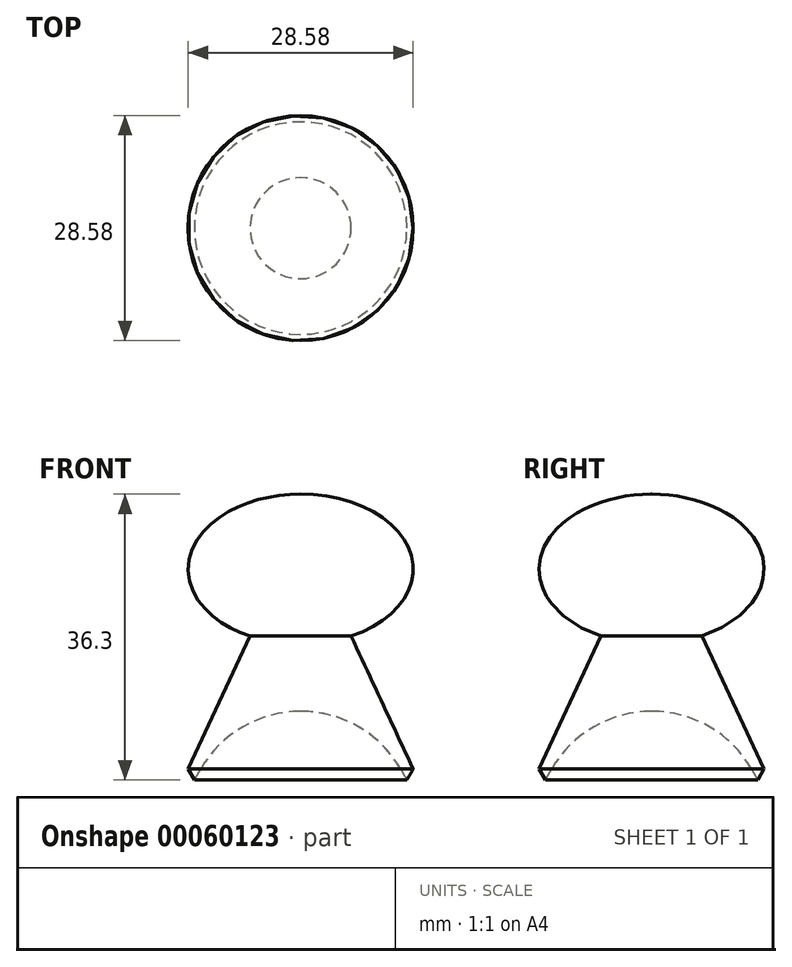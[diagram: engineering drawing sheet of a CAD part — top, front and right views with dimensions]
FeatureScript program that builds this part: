
annotation { "Feature Type Name" : "Feature", "Feature Type Description" : "" }
export const myFeature = defineFeature(function(context is Context, id is Id, definition is map)
    precondition{}
    {
        {
            var Q0;
            Q0=qCreatedBy(makeId("Front.planeOp"),FACE);
            var sketch = newSketch(context, id + "F0", { "sketchPlane" : qUnion([Q0])});
            skLineSegment(sketch, "E0", {"start": v(0, 25.4) * mm, "end": v(2.45, 25.4) * mm});
            skLineSegment(sketch, "E1", {"start": v(2.45, 25.4) * mm, "end": v(14.3, 0) * mm});
            skLineSegment(sketch, "E2", {"start": v(14.3, 0) * mm, "end": v(13.5, -1.37) * mm});
            skLineSegment(sketch, "E3", {"start": v(13.5, -1.37) * mm, "end": v(12.7, 0) * mm});
            skLineSegment(sketch, "E4", {"start": v(0, 25.4) * mm, "end": v(0, 25.4) * mm});
            skLineSegment(sketch, "E5", {"start": v(0, 84.03) * mm, "end": v(0, -77.86) * mm, "construction": true});
            skLineSegment(sketch, "E6.MirrorCS", {"start": v(-13.5, -1.37) * mm, "end": v(-12.7, 0) * mm});
            skLineSegment(sketch, "E7.MirrorCS", {"start": v(0, 25.4) * mm, "end": v(-2.45, 25.4) * mm});
            skLineSegment(sketch, "E8.MirrorCS", {"start": v(-2.45, 25.4) * mm, "end": v(-14.3, 0) * mm});
            skLineSegment(sketch, "E9.MirrorCS", {"start": v(-14.3, 0) * mm, "end": v(-13.5, -1.37) * mm});
            skEllipse(sketch, "E10", {"center": v(0, 25.4) * mm, "majorRadius": 14.3 * mm, "minorRadius": 9.53 * mm, "majorAxis": v(1, 0)});
            skLineSegment(sketch, "E11", {"start": v(0, 25.4) * mm, "end": v(14.3, 25.4) * mm, "construction": true});
            skArc(sketch, "E12", {"start": v(12.7, 0) * mm, "mid": v(7.34, 5.37) * mm, "end": v(0, 7.34) * mm});
            skArc(sketch, "E13.MirrorCS", {"start": v(-12.7, 0) * mm, "mid": v(-7.34, 5.37) * mm, "end": v(0, 7.34) * mm});
            skLineSegment(sketch, "E14", {"start": v(0, 34.93) * mm, "end": v(0, 7.34) * mm});
            skSolve(sketch);
        }
        {
            var Q0;
            Q0=makeQuery(id+"F0.imprint","IMPRINT",FACE,{"disambiguationData":[TD([[makeQuery(id+"F0.imprint","IMPRINT",EDGE,{"derivedFrom":sQuery(id+"F0.wireOp",EDGE,"E0")}),-1.0]])]});
            var Q1;
            {var subQ0=sQuery(id+"F0.wireOp",EDGE,"E0");Q1=makeQuery(id+"F0.imprint","IMPRINT",FACE,{"disambiguationData":[TD([[makeQuery(id+"F0.imprint","IMPRINT",EDGE,{"derivedFrom":subQ0}),1.0]])]});}
            var Q2;
            {var subQ5=sQuery(id+"F0.wireOp",EDGE,"E2");Q2=makeQuery(id+"F0.imprint","IMPRINT",FACE,{"disambiguationData":[TD([[makeQuery(id+"F0.imprint","IMPRINT",EDGE,{"derivedFrom":subQ5}),-1.0]])]});}
            var Q3;
            Q3=sQuery(id+"F0.wireOp",EDGE,"E5");
            revolve(context, id + "F1", {"entities" : qUnion([Q0, Q1, Q2]), "axis" : qUnion([Q3]), "revolveType" : RevolveType.FULL});
        }
    });
